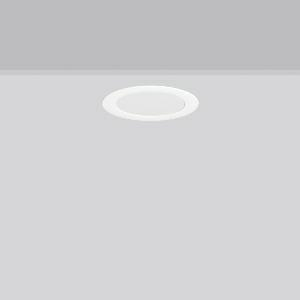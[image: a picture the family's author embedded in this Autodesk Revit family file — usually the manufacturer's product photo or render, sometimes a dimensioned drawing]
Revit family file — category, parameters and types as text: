
# Revit family: toledo_flat_round_e_672222_002_04_7e31
name_source: partatom
category: Lighting Fixtures
units: mm (PartAtom-declared; Revit-internal decimal feet)

## family parameters
Cut with Voids When Loaded = No
Host = Face
Light Source = No
Part Type = Normal
Room Calculation Point = No
Round Connector Dimension = Use Diameter
Shared = No

## types (1)
- TOLEDO FLAT round E (1 x LED Modul 830, 780 lm, 3000)
    Apparent Load = 8 VA
    CIE Flux Codes = 47 79 96 100 100
    Color Rendering = 80
    Color Temperature = 3000
    Default Elevation = 1800 mm
    Description = Series: TOLEDO FLAT round
Ultra thin recessed downlight. For escape route illumination. Housing: die-cast aluminium, powder-coated. Lightguide and diffuser made of non-yellowing plastic (PMMA). Diffuser opal matt plastic. Ceiling installation with spring system. Including separate LED converter with connecting cable 250 mm. Self-contained system with automatic self-test and feedback to the RZB monitoring system MULTIDIGIT. External driver with simple plug-in locking system. 
Colour: white
Diameter: 190 mm
Height: 2.5 mm
Cut-out diameter: 170 mm
Recess height: 120 mm
Luminaire: recess height: 60-80 mm
Weight: 1.41 kg
Operating mode: maintained power mode
Duration time: 3 h
Lamp: LED
Socket: without socket
Colour temperature: 3000K
Colour rendering index (CRI): 80
System power: 7.7 W
Rated luminous flux: 780 lm
Luminous flux, emergency: 350 lm
System power, emergency: -
Control gear: Regulated power supply
Protection class: I
Type of protection: IP 54
    Height = 0 mm  [stored 0 ft]
    Lamp = 1 x LED Modul 830
    Lamp Light Flux = 780 lm
    Lamp count = 1
    Length = 190 mm  [stored 0.62336 ft]
    Lifetime = 50000 h
    Luminous efficacy = 101 lm/W
    Manufacturer = RZB
    ModVariant = No
    Model = 672222.002.04
    Mounting Place = Ceiling
    Mounting Type = Recessed
    Number of Poles = 1
    OnlyDefault = Yes
    Power Factor = 1
    Product Name = TOLEDO FLAT round E
    Product group = Recessed downlights
    ProductGroupID = 402
    Protection Class = Protection class I
    Protection Degree = IP 40
    RLX_Detail_Level = 1
    RLX_Emergency_Light_Flux = 350 lm
    RLX_Emergency_Type = 3
    RLX_Emergency_Type_DB = Yes
    RlxData = <blob elided: 29361 chars, md5=37afa946>
    Socket = socket
    Standby Power = 0 W
    System Light Flux = 780 lm
    System Power = 8 W
    Type Comments = Product without accessories
    Type Image = 901452.002.jpg
    URL = http://relux.com
    VarID = ---
    Voltage = 230 V
    Voltage Range = 220-240 V
    Weight = 0.00 kg
    Width = 0 mm  [stored 0 ft]

note: [stored X ft] marks values corroborated as IEEE doubles in the binary element streams (Revit-internal decimal feet)

## geometry (parser evidence)
native form markers: Blend x4, Sweep x9
no freeform markers — native parametric forms only
